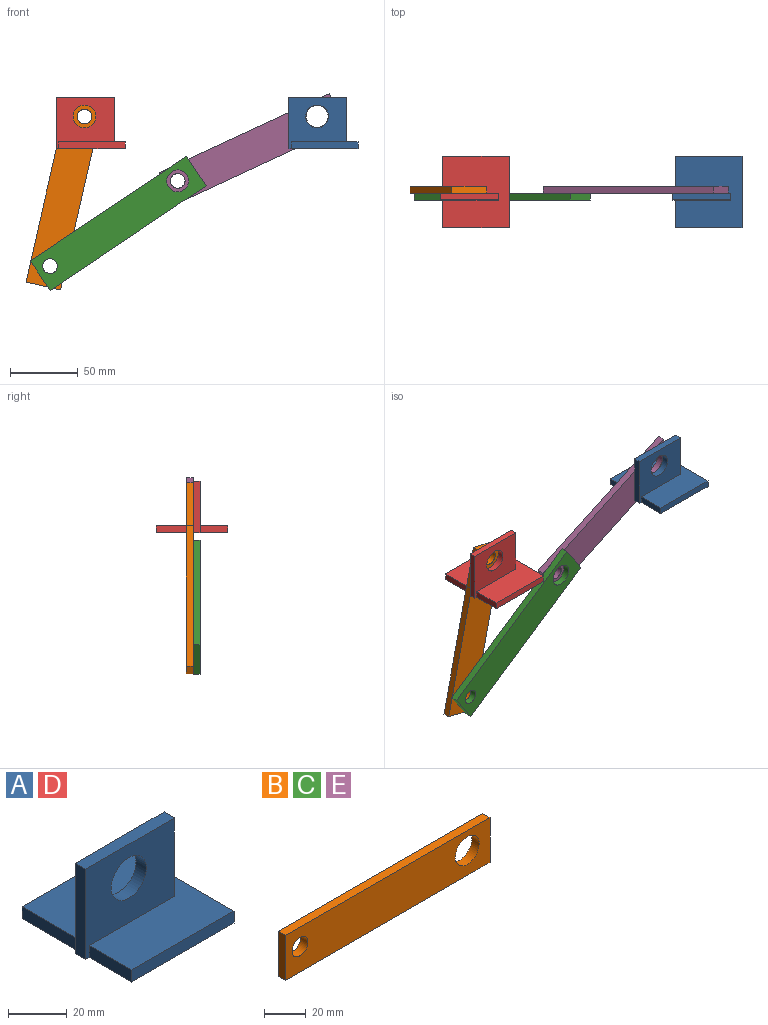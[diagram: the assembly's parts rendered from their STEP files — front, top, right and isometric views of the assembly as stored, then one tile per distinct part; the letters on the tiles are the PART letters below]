
ASSEMBLY  parts=5 mates=7
PART A: 13 faces, bbox 51.2x53.1x37.8 mm
  f0: plane 27.47x5mm, normal (-1,0,0), area 137.3mm2, adj f1,f5,f6,f8
  f1: plane 49.39x5mm, normal (0,1,0), area 246.9mm2, adj f0,f4,f5,f6
  f2: plane 20.61x5mm, normal (-1,0,0), area 103mm2, adj f3,f5,f6,f7
  f3: plane 49.39x5mm, normal (0,-1,0), area 246.9mm2, adj f2,f4,f5,f6
  f4: plane 53.08x5mm, normal (1,0,0), area 265.4mm2, adj f1,f3,f5,f6
  f5: plane 53.08x49.39mm, normal (0,0,1), area 2415.4mm2, adj f0,f1,f2,f3,f4,f7,f8,f10
  f6: plane 53.08x51.17mm, normal (0,0,-1), area 2630.4mm2, adj f0,f1,f2,f3,f4,f7,f8,f9
  f7: plane 43x37.76mm, normal (0,-1,0), area 1192mm2, adj f2,f5,f6,f9,f10,f11,f12
  f8: plane 43x37.76mm, normal (0,1,0), area 1192mm2, adj f0,f5,f6,f9,f10,f11,f12
  f9: plane 37.76x5mm, normal (-1,0,0), area 188.8mm2, adj f6,f7,f8,f11
  f10: plane 32.76x5mm, normal (1,0,0), area 163.8mm2, adj f5,f7,f8,f11
  f11: plane 43x5mm, normal (0,0,1), area 215mm2, adj f7,f8,f9,f10
  f12: cylinder r=8.48mm len=16.95mm, axis (0,1,0), area 266.3mm2, adj f7,f8
PART B: 8 faces, bbox 138.9x5x26.5 mm
  f0: plane 138.93x5mm, normal (0,0,1), area 694.6mm2, adj f1,f5,f6,f7
  f1: plane 26.46x5mm, normal (-1,0,0), area 132.3mm2, adj f0,f2,f6,f7
  f2: plane 138.93x5mm, normal (0,0,-1), area 694.6mm2, adj f1,f5,f6,f7
  f3: cylinder r=5.41mm len=10.83mm, axis (0,1,0), area 170mm2, adj f6,f7
  f4: cylinder r=8.12mm len=16.24mm, axis (0,1,0), area 255.1mm2, adj f6,f7
  f5: plane 26.24x5mm, normal (1,0,0), area 131.2mm2, adj f0,f2,f6,f7
  f6: plane 138.93x26.46mm, normal (0,-1,0), area 3361.7mm2, adj f0,f1,f2,f3,f4,f5
  f7: plane 138.93x26.46mm, normal (0,1,0), area 3361.7mm2, adj f0,f1,f2,f3,f4,f5
PART C: same geometry as B
PART D: same geometry as A
PART E: same geometry as B
PLACE A t=(-107.62,-102.6,19.18)mm fixed
PLACE B rot(axis=(0,1,0),102.8deg) t=(-341.17,-97.6,-52.49)mm
PLACE C rot(axis=(0,-1,0),33.9deg) t=(-211.71,-102.6,-33.98)mm
PLACE D t=(-279.7,-102.6,19.18)mm fixed
PLACE E rot(axis=(0,-1,0),24.9deg) t=(-113.25,-97.6,12.64)mm
MATE revolute B.f3 <-> D.f12  axis (0,-1,0) through (-289.34,-102.6,42.86)mm
MATE planar B.f6 <-> D.f8  axis (0,-1,0) through (-317.17,-102.6,-11.87)mm
MATE revolute E.f3 <-> C.f4  axis (0,-1,0) through (-220.37,-102.6,-4.76)mm
MATE revolute C.f3 <-> B.f4  axis (0,1,0) through (-314.83,-102.6,-67.82)mm
MATE revolute E.f4 <-> A.f12  axis (0,-1,0) through (-117.27,-102.6,42.86)mm
MATE planar A.f5 <-> D.f5  axis (0,0,1) through (-111.39,-101.38,24.18)mm
MATE planar D.f7 <-> A.f7  axis (0,-1,0) through (-308.51,-107.6,24.18)mm
